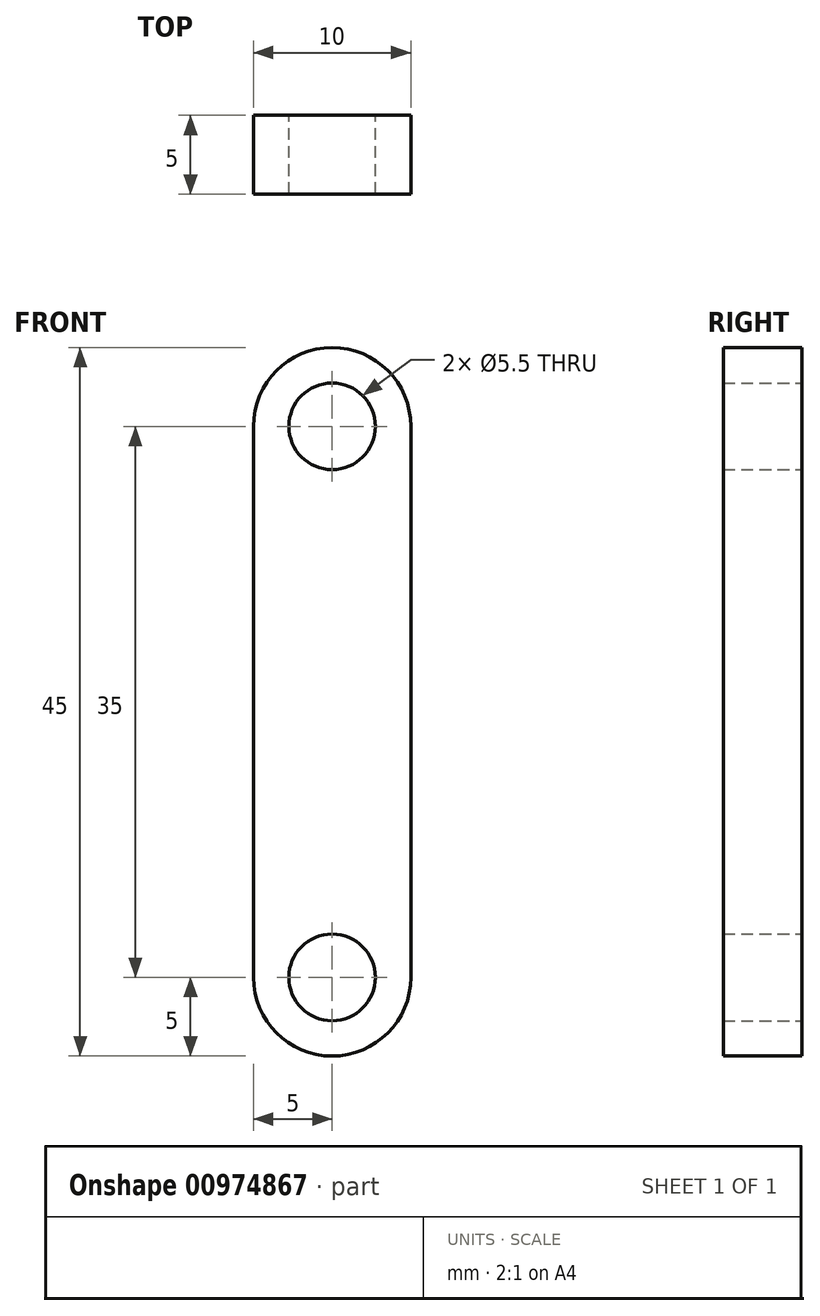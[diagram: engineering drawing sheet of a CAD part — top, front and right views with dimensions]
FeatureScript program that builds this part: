
annotation { "Feature Type Name" : "Feature", "Feature Type Description" : "" }
export const myFeature = defineFeature(function(context is Context, id is Id, definition is map)
    precondition{}
    {
        {
            var Q0;
            Q0=qCreatedBy(makeId("Front.planeOp"),FACE);
            var sketch = newSketch(context, id + "F0", { "sketchPlane" : qUnion([Q0])});
            skArc(sketch, "E0", {"start": v(5, 17.5) * mm, "mid": v(0, 22.5) * mm, "end": v(-5, 17.5) * mm});
            skArc(sketch, "E1.MirrorC", {"start": v(5, -17.5) * mm, "mid": v(0, -22.5) * mm, "end": v(-5, -17.5) * mm});
            skLineSegment(sketch, "E2", {"start": v(5, 17.5) * mm, "end": v(5, -17.5) * mm});
            skLineSegment(sketch, "E3", {"start": v(-5, -17.5) * mm, "end": v(-5, 17.5) * mm});
            skCircle(sketch, "E4", {"center": v(0, 17.5) * mm, "radius": 2.75 * mm});
            skCircle(sketch, "E5.MirrorC", {"center": v(0, -17.5) * mm, "radius": 2.75 * mm});
            skSolve(sketch);
        }
        {
            var Q0;
            Q0=qSketchRegion(id+"F0",true);
            extrude(context, id + "F1", {"entities" : qUnion([Q0]), "depth" : 5 * mm, "offsetDistance" : 25 * mm});
        }
    });
